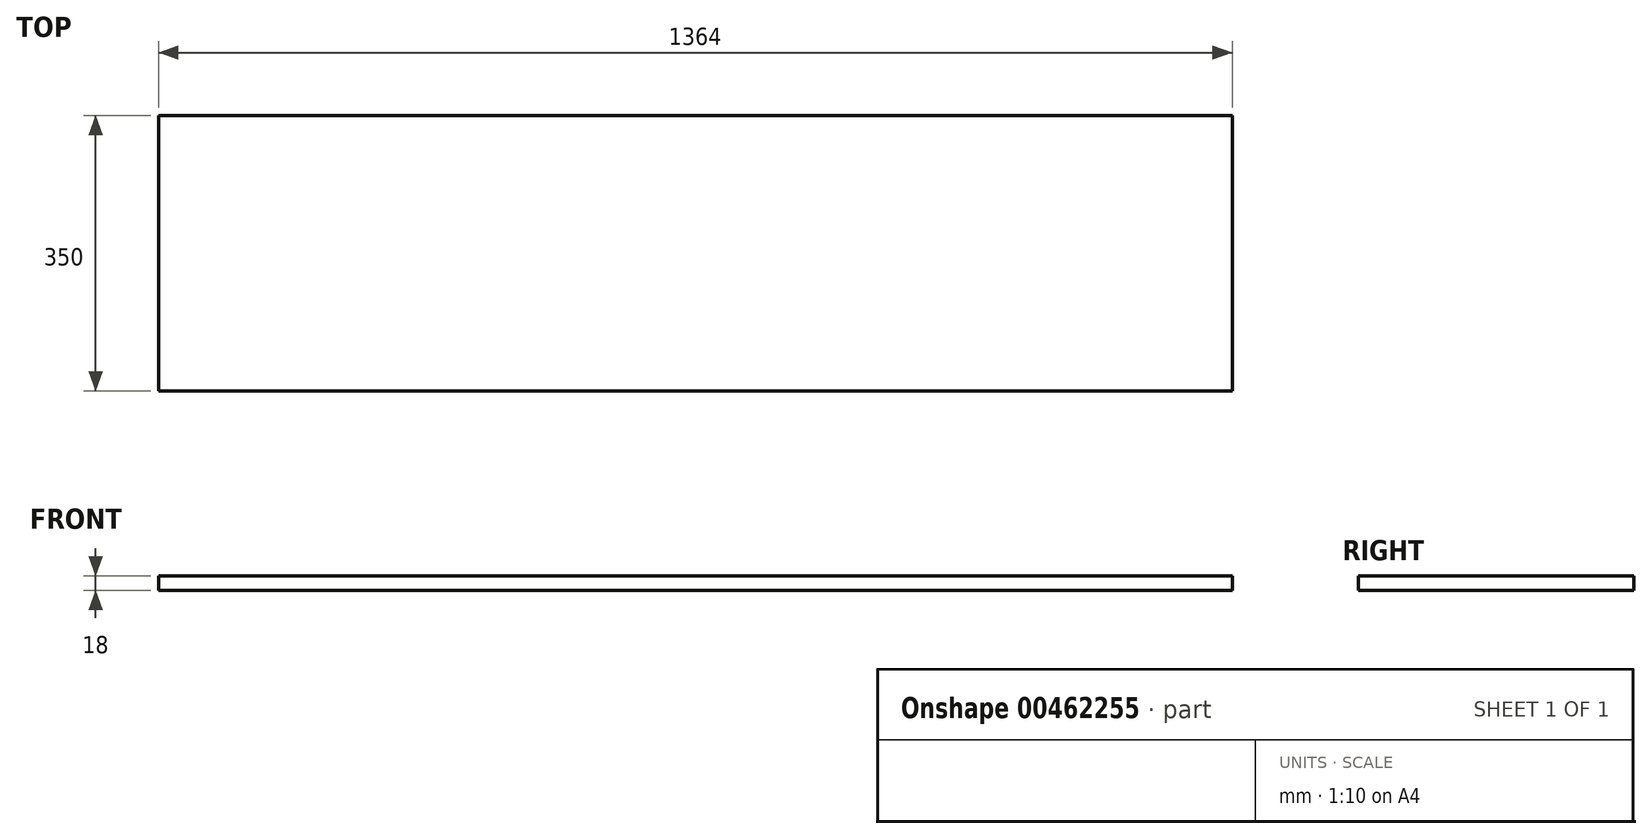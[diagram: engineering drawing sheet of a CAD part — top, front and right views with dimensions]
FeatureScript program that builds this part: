
annotation { "Feature Type Name" : "Feature", "Feature Type Description" : "" }
export const myFeature = defineFeature(function(context is Context, id is Id, definition is map)
    precondition{}
    {
        {
            var Q0;
            Q0=qCreatedBy(makeId("Top.planeOp"),FACE);
            var sketch = newSketch(context, id + "F0", { "sketchPlane" : qUnion([Q0])});
            skLineSegment(sketch, "E0.bottom", {"start": v(682, -175) * mm, "end": v(-682, -175) * mm});
            skLineSegment(sketch, "E0.top", {"start": v(682, 175) * mm, "end": v(-682, 175) * mm});
            skLineSegment(sketch, "E0.left", {"start": v(682, -175) * mm, "end": v(682, 175) * mm});
            skLineSegment(sketch, "E0.right", {"start": v(-682, -175) * mm, "end": v(-682, 175) * mm});
            skPoint(sketch, "E0.middle", {"position": v(0, 0) * mm});
            skSolve(sketch);
        }
        {
            var Q0;
            Q0=makeQuery(id+"F0.imprint","IMPRINT",FACE,{"disambiguationData":[TD([[makeQuery(id+"F0.imprint","IMPRINT",EDGE,{"derivedFrom":sQuery(id+"F0.wireOp",EDGE,"E0.bottom")}),-1.0]])]});
            extrude(context, id + "F1", {"entities" : qUnion([Q0]), "depth" : 18 * mm});
        }
    });
